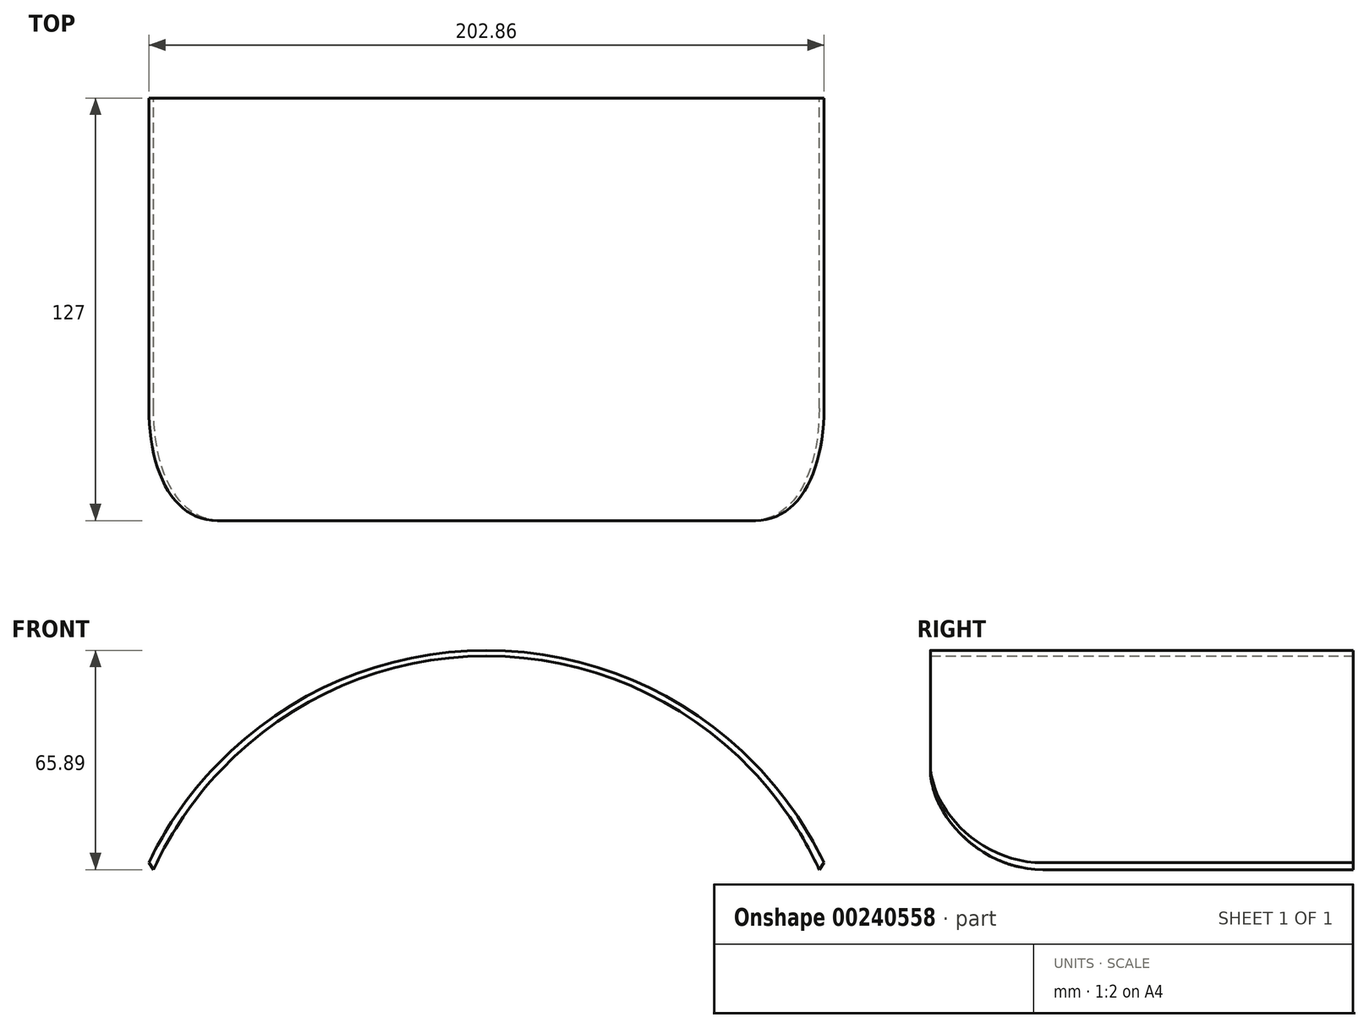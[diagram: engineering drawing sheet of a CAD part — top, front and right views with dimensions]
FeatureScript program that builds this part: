
annotation { "Feature Type Name" : "Feature", "Feature Type Description" : "" }
export const myFeature = defineFeature(function(context is Context, id is Id, definition is map)
    precondition{}
    {
        {
            var Q0;
            Q0=qCreatedBy(makeId("Front.planeOp"),FACE);
            var sketch = newSketch(context, id + "F0", { "sketchPlane" : qUnion([Q0])});
            skArc(sketch, "E0", {"start": v(200, 0) * mm, "mid": v(100, 64.17) * mm, "end": v(0, 0) * mm});
            skLineSegment(sketch, "E1", {"start": v(0, 0) * mm, "end": v(-1.43, 2.05) * mm});
            skLineSegment(sketch, "E2", {"start": v(200, 0) * mm, "end": v(201.43, 2.05) * mm});
            skArc(sketch, "E3", {"start": v(201.43, 2.05) * mm, "mid": v(100, 65.9) * mm, "end": v(-1.43, 2.05) * mm});
            skSolve(sketch);
        }
        {
            var Q0;
            Q0=makeQuery(id+"F0.imprint","IMPRINT",FACE,{"disambiguationData":[TD([[makeQuery(id+"F0.imprint","IMPRINT",EDGE,{"derivedFrom":sQuery(id+"F0.wireOp",EDGE,"E0")}),-1.0]])]});
            extrude(context, id + "F1", {"entities" : qUnion([Q0]), "depth" : 127 * mm});
        }
        {
            var Q0;
            Q0=makeQuery(id+"F1.opExtrude","CAP_EDGE",EDGE,{"disambiguationData":[OSD([sQuery(id+"F0.wireOp",EDGE,"E2")])],"isStart":false});
            var Q1;
            Q1=makeQuery(id+"F1.opExtrude","CAP_EDGE",EDGE,{"disambiguationData":[OSD([sQuery(id+"F0.wireOp",EDGE,"E1")])],"isStart":false});
            fillet(context, id + "F2", {"entities" : qUnion([Q0, Q1]), "radius" : 33.8 * mm, "tangentPropagation" : true, "allowEdgeOverflow" : false});
        }
    });
